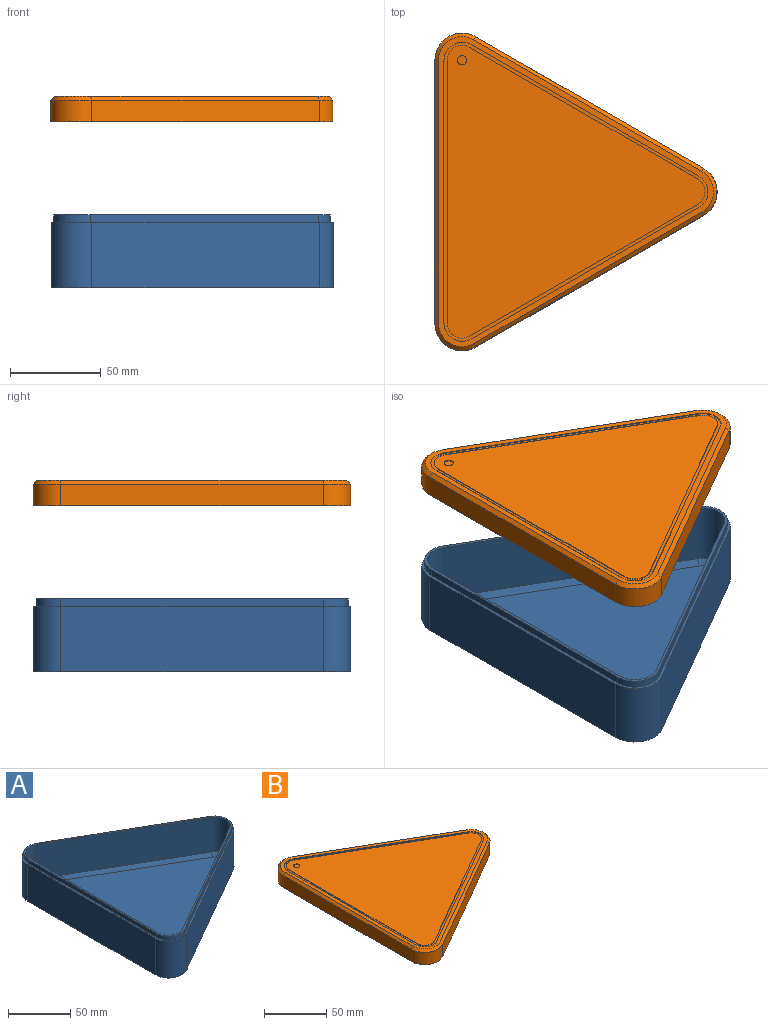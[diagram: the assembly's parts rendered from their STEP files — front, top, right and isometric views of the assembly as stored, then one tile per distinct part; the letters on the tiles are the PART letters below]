
ASSEMBLY  parts=2 mates=1
PART A: 28 faces, bbox 155.5x174.9x40 mm
  f0: plane 171.93x152.51mm, normal (0,0,1), area 772.3mm2, adj f1,f2,f3,f4,f5,f6,f14,f15
  f1: cylinder r=12mm len=34mm, axis (0,0,-1), area 854.5mm2, adj f0,f2,f6,f10
  f2: plane 125.51x72.46mm, normal (-0.5,-0.87,0), area 4927.5mm2, adj f0,f1,f3,f8
  f3: cylinder r=12mm len=34mm, axis (0,0,-1), area 854.5mm2, adj f0,f2,f4,f9
  f4: plane 144.93x34mm, normal (1,0,0), area 4927.5mm2, adj f0,f3,f5,f11
  f5: cylinder r=12mm len=34mm, axis (0,0,-1), area 854.5mm2, adj f0,f4,f6,f13
  f6: plane 125.51x72.46mm, normal (-0.5,0.87,0), area 4927.5mm2, adj f0,f1,f5,f12
  f7: plane 162.93x143.51mm, normal (0,0,1), area 13262.3mm2, adj f8,f9,f10,f11,f12,f13
  f8: plane 127.01x75.06mm, normal (-0.35,-0.61,0.71), area 614.9mm2, adj f2,f7,f9,f10
  f9: cone r=9mm half-angle=45deg, axis (0,0,1), area 93.3mm2, adj f3,f7,f8,f11
  f10: cone r=9mm half-angle=45deg, axis (0,0,1), area 93.3mm2, adj f1,f7,f8,f12
  f11: plane 144.93x3mm, normal (0.71,0,0.71), area 614.9mm2, adj f4,f7,f9,f13
  f12: plane 127.01x75.06mm, normal (-0.35,0.61,0.71), area 614.9mm2, adj f6,f7,f10,f13
  f13: cone r=9mm half-angle=45deg, axis (0,0,1), area 93.3mm2, adj f5,f7,f11,f12
  f14: cylinder r=13.5mm len=20.25mm, axis (0,0,1), area 113.1mm2, adj f0,f15,f19,f20
  f15: plane 125.51x72.46mm, normal (0.5,0.87,0), area 579.7mm2, adj f0,f14,f16,f20
  f16: cylinder r=13.5mm len=23.38mm, axis (0,0,1), area 113.1mm2, adj f0,f15,f17,f20
  f17: plane 125.51x72.46mm, normal (0.5,-0.87,0), area 579.7mm2, adj f0,f16,f18,f20
  f18: cylinder r=13.5mm len=20.25mm, axis (0,0,1), area 113.1mm2, adj f0,f17,f19,f20
  f19: plane 144.93x4mm, normal (-1,0,0), area 579.7mm2, adj f0,f14,f18,f20
  f20: plane 174.93x155.51mm, normal (0,0,1), area 786.5mm2, adj f14,f15,f16,f17,f18,f19,f22,f23
  f21: plane 174.93x155.51mm, normal (0,0,-1), area 16323.3mm2, adj f22,f23,f24,f25,f26,f27
  f22: plane 125.51x72.46mm, normal (0.5,-0.87,0), area 5217.3mm2, adj f20,f21,f23,f27
  f23: cylinder r=15mm len=36mm, axis (0,0,-1), area 1131mm2, adj f20,f21,f22,f24
  f24: plane 144.93x36mm, normal (-1,0,0), area 5217.3mm2, adj f20,f21,f23,f25
  f25: cylinder r=15mm len=36mm, axis (0,0,-1), area 1131mm2, adj f20,f21,f24,f26
  f26: plane 125.51x72.46mm, normal (0.5,0.87,0), area 5217.3mm2, adj f20,f21,f25,f27
  f27: cylinder r=15mm len=36mm, axis (0,0,-1), area 1131mm2, adj f20,f21,f22,f26
PART B: 50 faces, bbox 155.5x174.9x14 mm
  f0: plane 171.93x152.51mm, normal (0,0,-1), area 772.3mm2, adj f2,f3,f4,f5,f6,f7,f14,f15
  f1: plane 162.93x143.51mm, normal (0,0,-1), area 13262.3mm2, adj f8,f9,f10,f11,f12,f13
  f2: plane 125.51x72.46mm, normal (-0.5,0.87,0), area 579.7mm2, adj f0,f3,f7,f12
  f3: cylinder r=12mm len=18mm, axis (0,0,-1), area 100.5mm2, adj f0,f2,f4,f13
  f4: plane 144.93x4mm, normal (1,0,0), area 579.7mm2, adj f0,f3,f5,f11
  f5: cylinder r=12mm len=18mm, axis (0,0,-1), area 100.5mm2, adj f0,f4,f6,f9
  f6: plane 125.51x72.46mm, normal (-0.5,-0.87,0), area 579.7mm2, adj f0,f5,f7,f8
  f7: cylinder r=12mm len=20.78mm, axis (0,0,-1), area 100.5mm2, adj f0,f2,f6,f10
  f8: plane 127.01x75.06mm, normal (-0.35,-0.61,-0.71), area 614.9mm2, adj f1,f6,f9,f10
  f9: cone r=12mm half-angle=45deg, axis (0,0,-1), area 93.3mm2, adj f1,f5,f8,f11
  f10: cone r=12mm half-angle=45deg, axis (0,0,-1), area 93.3mm2, adj f1,f7,f8,f12
  f11: plane 144.93x3mm, normal (0.71,0,-0.71), area 614.9mm2, adj f1,f4,f9,f13
  f12: plane 127.01x75.06mm, normal (-0.35,0.61,-0.71), area 614.9mm2, adj f1,f2,f10,f13
  f13: cone r=12mm half-angle=45deg, axis (0,0,-1), area 93.3mm2, adj f1,f3,f11,f12
  f14: cylinder r=13.5mm len=20.25mm, axis (0,0,1), area 113.1mm2, adj f0,f15,f19,f20
  f15: plane 125.51x72.46mm, normal (-0.5,-0.87,0), area 579.7mm2, adj f0,f14,f16,f20
  f16: cylinder r=13.5mm len=23.38mm, axis (0,0,1), area 113.1mm2, adj f0,f15,f17,f20
  f17: plane 125.51x72.46mm, normal (-0.5,0.87,0), area 579.7mm2, adj f0,f16,f18,f20
  f18: cylinder r=13.5mm len=20.25mm, axis (0,0,1), area 113.1mm2, adj f0,f17,f19,f20
  f19: plane 144.93x4mm, normal (1,0,0), area 579.7mm2, adj f0,f14,f18,f20
  f20: plane 174.93x155.51mm, normal (0,0,-1), area 786.5mm2, adj f14,f15,f16,f17,f18,f19,f28,f29
  f21: plane 170.93x151.51mm, normal (0,0,1), area 1521.1mm2, adj f22,f23,f24,f25,f26,f27,f34,f35
  f22: plane 126.51x74.2mm, normal (0.35,-0.61,0.71), area 409.9mm2, adj f21,f23,f27,f33
  f23: cone r=13mm half-angle=45deg, axis (0,0,-1), area 82.9mm2, adj f21,f22,f24,f32
  f24: plane 144.93x2mm, normal (-0.71,0,0.71), area 409.9mm2, adj f21,f23,f25,f31
  f25: cone r=13mm half-angle=45deg, axis (0,0,-1), area 82.9mm2, adj f21,f24,f26,f30
  f26: plane 126.51x74.2mm, normal (0.35,0.61,0.71), area 409.9mm2, adj f21,f25,f27,f29
  f27: cone r=13mm half-angle=45deg, axis (0,0,-1), area 82.9mm2, adj f21,f22,f26,f28
  f28: cylinder r=15mm len=25.98mm, axis (0,0,-1), area 377mm2, adj f20,f27,f29,f33
  f29: plane 125.51x72.46mm, normal (0.5,0.87,0), area 1739.1mm2, adj f20,f26,f28,f30
  f30: cylinder r=15mm len=22.5mm, axis (0,0,-1), area 377mm2, adj f20,f25,f29,f31
  f31: plane 144.93x12mm, normal (-1,0,0), area 1739.1mm2, adj f20,f24,f30,f32
  f32: cylinder r=15mm len=22.5mm, axis (0,0,-1), area 377mm2, adj f20,f23,f31,f33
  f33: plane 125.51x72.46mm, normal (0.5,-0.87,0), area 1739.1mm2, adj f20,f22,f28,f32
  f34: plane 125.51x72.46mm, normal (-0.5,-0.87,0), area 58mm2, adj f21,f35,f45,f46
  f35: cylinder r=10mm len=15mm, axis (0,0,1), area 8.4mm2, adj f21,f34,f36,f46
  f36: plane 144.93x0.4mm, normal (1,0,0), area 58mm2, adj f21,f35,f37,f46
  f37: cylinder r=10mm len=15mm, axis (0,0,1), area 8.4mm2, adj f21,f36,f38,f46
  f38: plane 125.51x72.46mm, normal (-0.5,0.87,0), area 58mm2, adj f21,f37,f45,f46
  f39: cylinder r=8.2mm len=12.3mm, axis (0,0,1), area 6.9mm2, adj f40,f44,f46,f47
  f40: plane 125.51x72.46mm, normal (0.5,0.87,0), area 58mm2, adj f39,f41,f46,f47
  f41: cylinder r=8.2mm len=14.2mm, axis (0,0,1), area 6.9mm2, adj f40,f42,f46,f47
  f42: plane 125.51x72.46mm, normal (0.5,-0.87,0), area 58mm2, adj f41,f43,f46,f47
  f43: cylinder r=8.2mm len=12.3mm, axis (0,0,1), area 6.9mm2, adj f42,f44,f46,f47
  f44: plane 144.93x0.4mm, normal (-1,0,0), area 58mm2, adj f39,f43,f46,f47
  f45: cylinder r=10mm len=17.32mm, axis (0,0,1), area 8.4mm2, adj f21,f34,f38,f46
  f46: plane 164.93x145.51mm, normal (0,0,1), area 885.5mm2, adj f34,f35,f36,f37,f38,f39,f40,f41
  f47: plane 161.33x141.91mm, normal (0,0,1), area 12851.6mm2, adj f39,f40,f41,f42,f43,f44,f48
  f48: cylinder r=2.5mm len=5mm, axis (0,0,1), area 6.3mm2, adj f47,f49
  f49: plane 5x5mm, normal (0,0,1), area 19.6mm2, adj f48
PLACE A t=(-114.95,27.32,89.23)mm
PLACE B t=(-115.01,27.43,144.55)mm
MATE slider B.f47 <-> A.f21  axis (0,0,1) through (-114.95,27.32,169.55)mm
